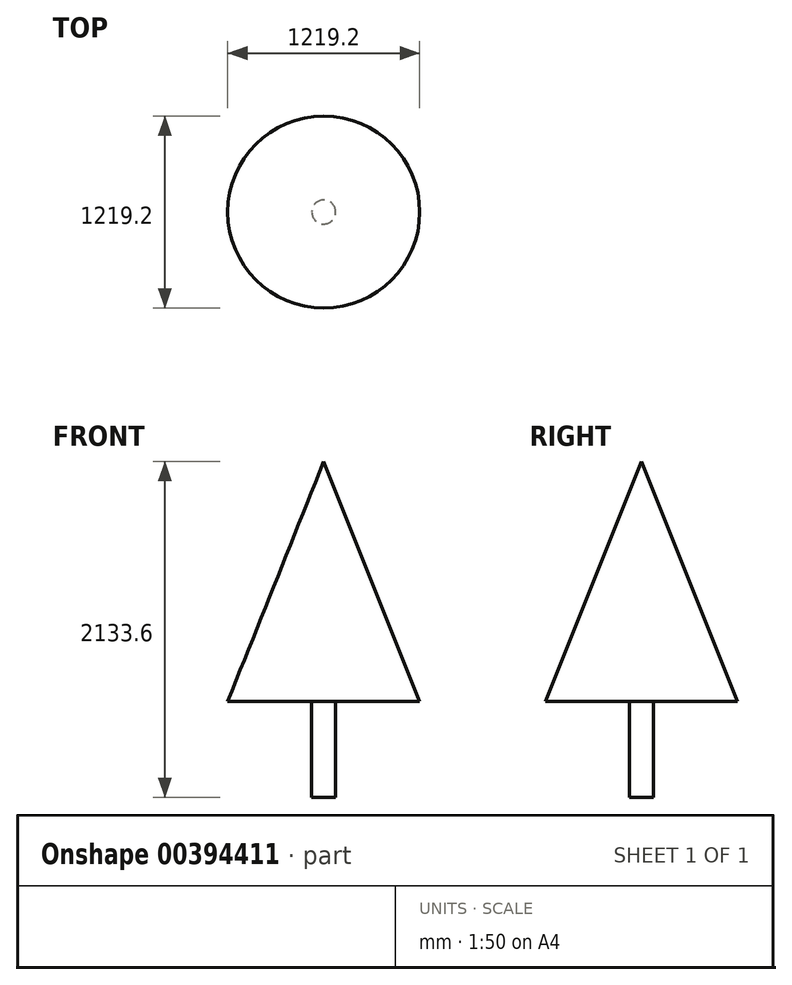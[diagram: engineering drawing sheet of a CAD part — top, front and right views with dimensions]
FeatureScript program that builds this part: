
annotation { "Feature Type Name" : "Feature", "Feature Type Description" : "" }
export const myFeature = defineFeature(function(context is Context, id is Id, definition is map)
    precondition{}
    {
        {
            var Q0;
            Q0=qCreatedBy(makeId("Front.planeOp"),FACE);
            var sketch = newSketch(context, id + "F0", { "sketchPlane" : qUnion([Q0])});
            skLineSegment(sketch, "E0.bottom", {"start": v(0, 0) * mm, "end": v(-76.2, 0) * mm});
            skLineSegment(sketch, "E0.top", {"start": v(0, -609.6) * mm, "end": v(-76.2, -609.6) * mm});
            skLineSegment(sketch, "E0.left", {"start": v(0, 0) * mm, "end": v(0, -609.6) * mm});
            skLineSegment(sketch, "E0.right", {"start": v(-76.2, 0) * mm, "end": v(-76.2, -609.6) * mm});
            skSolve(sketch);
        }
        {
            var Q0;
            Q0 = qSketchRegion(id + "F0", true);
            var Q1;
            Q1=sQuery(id+"F0.wireOp",EDGE,"E0.left");
            revolve(context, id + "F1", {"entities" : qUnion([Q0]), "axis" : qUnion([Q1]), "revolveType" : RevolveType.FULL});
        }
        {
            var Q0;
            Q0=qCreatedBy(makeId("Front.planeOp"),FACE);
            var sketch = newSketch(context, id + "F2", { "sketchPlane" : qUnion([Q0])});
            skLineSegment(sketch, "E1", {"start": v(0, 0) * mm, "end": v(-609.6, 0) * mm});
            skLineSegment(sketch, "E2", {"start": v(-609.6, 0) * mm, "end": v(0, 1524) * mm});
            skLineSegment(sketch, "E3", {"start": v(0, 1524) * mm, "end": v(0, 0) * mm});
            skSolve(sketch);
        }
        {
            var Q0;
            Q0=makeQuery(id+"F2.imprint","IMPRINT",FACE,{"disambiguationData":[TD([[makeQuery(id+"F2.imprint","IMPRINT",EDGE,{"derivedFrom":sQuery(id+"F2.wireOp",EDGE,"E1")}),-1.0]])]});
            var Q1;
            Q1=sQuery(id+"F2.wireOp",EDGE,"E3");
            revolve(context, id + "F3", {"operationType" : NewBodyOperationType.ADD, "entities" : qUnion([Q0]), "axis" : qUnion([Q1]), "revolveType" : RevolveType.FULL});
        }
    });
